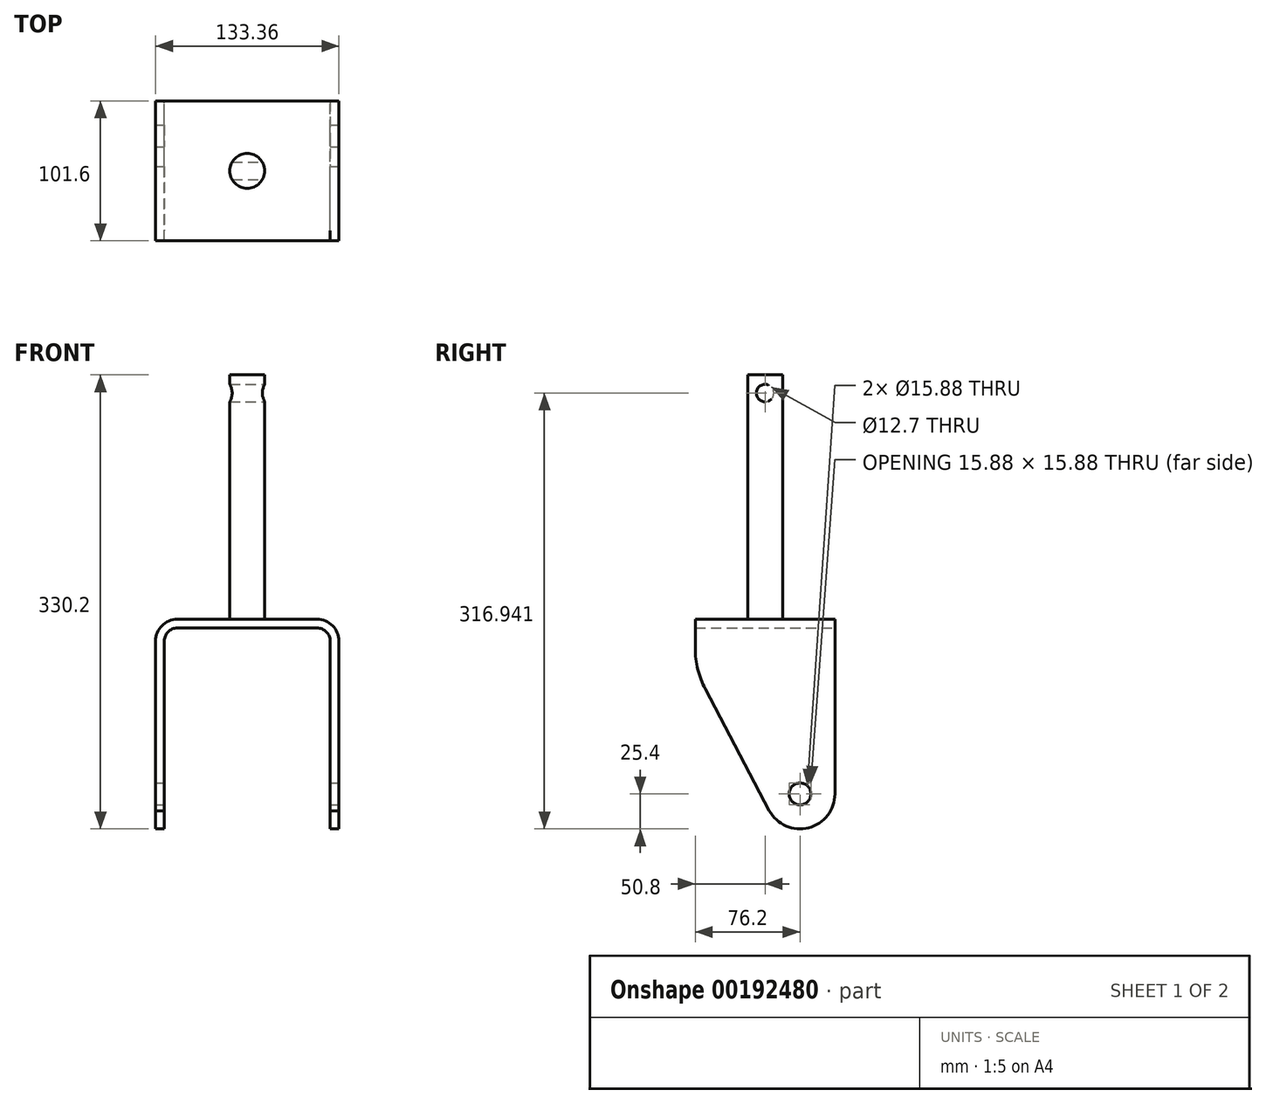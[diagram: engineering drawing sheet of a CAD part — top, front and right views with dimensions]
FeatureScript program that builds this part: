
annotation { "Feature Type Name" : "Feature", "Feature Type Description" : "" }
export const myFeature = defineFeature(function(context is Context, id is Id, definition is map)
    precondition{}
    {
        {
            var Q0;
            Q0=qCreatedBy(makeId("Front.planeOp"),FACE);
            var sketch = newSketch(context, id + "F0", { "sketchPlane" : qUnion([Q0])});
            skLineSegment(sketch, "E0", {"start": v(-66.67, 0) * mm, "end": v(-66.67, 136.53) * mm});
            skLineSegment(sketch, "E1", {"start": v(-50.8, 152.4) * mm, "end": v(50.8, 152.4) * mm});
            skLineSegment(sketch, "E2", {"start": v(66.68, 136.53) * mm, "end": v(66.68, 0) * mm});
            skLineSegment(sketch, "E3", {"start": v(60.33, 0) * mm, "end": v(66.68, 0) * mm});
            skLineSegment(sketch, "E4", {"start": v(60.33, 0) * mm, "end": v(60.33, 136.53) * mm});
            skLineSegment(sketch, "E5", {"start": v(50.8, 146.05) * mm, "end": v(-50.8, 146.05) * mm});
            skLineSegment(sketch, "E6", {"start": v(-60.32, 136.53) * mm, "end": v(-60.32, 0) * mm});
            skLineSegment(sketch, "E7", {"start": v(-66.67, 0) * mm, "end": v(-60.32, 0) * mm});
            skPoint(sketch, "E8.visualSharp", {"position": v(-60.32, 146.05) * mm});
            skArc(sketch, "E8.filletArc", {"start": v(-50.8, 146.05) * mm, "mid": v(-57.54, 143.26) * mm, "end": v(-60.33, 136.53) * mm});
            skPoint(sketch, "E9.visualSharp", {"position": v(60.33, 146.05) * mm});
            skArc(sketch, "E9.filletArc", {"start": v(60.33, 136.53) * mm, "mid": v(57.54, 143.26) * mm, "end": v(50.8, 146.05) * mm});
            skArc(sketch, "E10", {"start": v(-50.8, 152.4) * mm, "mid": v(-62.03, 147.75) * mm, "end": v(-66.68, 136.53) * mm});
            skArc(sketch, "E11", {"start": v(66.68, 136.53) * mm, "mid": v(62.03, 147.75) * mm, "end": v(50.8, 152.4) * mm});
            skLineSegment(sketch, "E12", {"start": v(0, 161.32) * mm, "end": v(0, 130.14) * mm, "construction": true});
            skPoint(sketch, "E12.startSnap0", {"position": v(0, 152.4) * mm});
            skPoint(sketch, "E12.endSnap0", {"position": v(0, 146.05) * mm});
            skLineSegment(sketch, "E13", {"start": v(0, 130.14) * mm, "end": v(0, 0) * mm, "construction": true});
            skSolve(sketch);
        }
        {
            var Q0;
            Q0 = qSketchRegion(id + "F0", true);
            extrude(context, id + "F1", {"entities" : qUnion([Q0]), "depth" : 101.6 * mm});
        }
        {
            var Q0;
            Q0=makeQuery(id+"F1.opExtrude","SWEPT_FACE",FACE,{"disambiguationData":[OSD([sQuery(id+"F0.wireOp",EDGE,"E1")])]});
            var sketch = newSketch(context, id + "F2", { "sketchPlane" : qUnion([Q0])});
            skLineSegment(sketch, "E14", {"start": v(-50.8, -101.6) * mm, "end": v(50.8, 0) * mm, "construction": true});
            skLineSegment(sketch, "E15", {"start": v(-50.8, 0) * mm, "end": v(50.8, -101.6) * mm, "construction": true});
            skCircle(sketch, "E16", {"center": v(0, -50.8) * mm, "radius": 12.7 * mm});
            skSolve(sketch);
        }
        {
            var Q0;
            Q0 = qSketchRegion(id + "F2", true);
            extrude(context, id + "F3", {"entities" : qUnion([Q0]), "operationType" : NewBodyOperationType.ADD, "depth" : 177.8 * mm});
        }
        {
            var Q0;
            Q0=makeQuery(id+"F1.opExtrude","SWEPT_FACE",FACE,{"disambiguationData":[OSD([sQuery(id+"F0.wireOp",EDGE,"E2")])]});
            var sketch = newSketch(context, id + "F4", { "sketchPlane" : qUnion([Q0])});
            skLineSegment(sketch, "E17", {"start": v(-101.6, 0) * mm, "end": v(-25.4, 0) * mm});
            skPoint(sketch, "E18.visualSharp", {"position": v(0, 0) * mm});
            skArc(sketch, "E18.filletArc", {"start": v(-25.4, 0) * mm, "mid": v(-7.44, 7.44) * mm, "end": v(0, 25.4) * mm});
            skArc(sketch, "E19", {"start": v(-48.07, 13.95) * mm, "mid": v(-19.51, 0.7) * mm, "end": v(0, 25.4) * mm});
            skLineSegment(sketch, "E20", {"start": v(-47.68, 13.2) * mm, "end": v(-94.3, 101.76) * mm});
            skLineSegment(sketch, "E21", {"start": v(-101.6, 131.34) * mm, "end": v(-101.6, 136.53) * mm});
            skCircle(sketch, "E22", {"center": v(-25.4, 25.4) * mm, "radius": 7.94 * mm});
            skPoint(sketch, "E23.visualSharp", {"position": v(-101.6, 115.65) * mm});
            skArc(sketch, "E23.filletArc", {"start": v(-101.6, 131.34) * mm, "mid": v(-99.75, 116.1) * mm, "end": v(-94.3, 101.76) * mm});
            skLineSegment(sketch, "E24", {"start": v(-101.6, 131.34) * mm, "end": v(-101.6, 0) * mm});
            skLineSegment(sketch, "E25", {"start": v(0, 0) * mm, "end": v(0, 25.4) * mm});
            skCircle(sketch, "E26", {"center": v(-50.8, 316.94) * mm, "radius": 6.35 * mm});
            skPoint(sketch, "E26.centerSnap0", {"position": v(-50.8, 136.53) * mm});
            skSolve(sketch);
        }
        {
            var Q0;
            Q0 = qSketchRegion(id + "F4", true);
            var Q1;
            {var subQ4=sQuery(id+"F4.wireOp",EDGE,"E25");Q1=makeQuery(id+"F4.imprint","IMPRINT",FACE,{"disambiguationData":[TD([[makeQuery(id+"F4.imprint","IMPRINT",EDGE,{"derivedFrom":subQ4}),-1.0]])]});}
            extrude(context, id + "F5", {"entities" : qUnion([Q0, Q1]), "operationType" : NewBodyOperationType.REMOVE, "oppositeDirection" : true, "depth" : 177.8 * mm});
        }
    });
